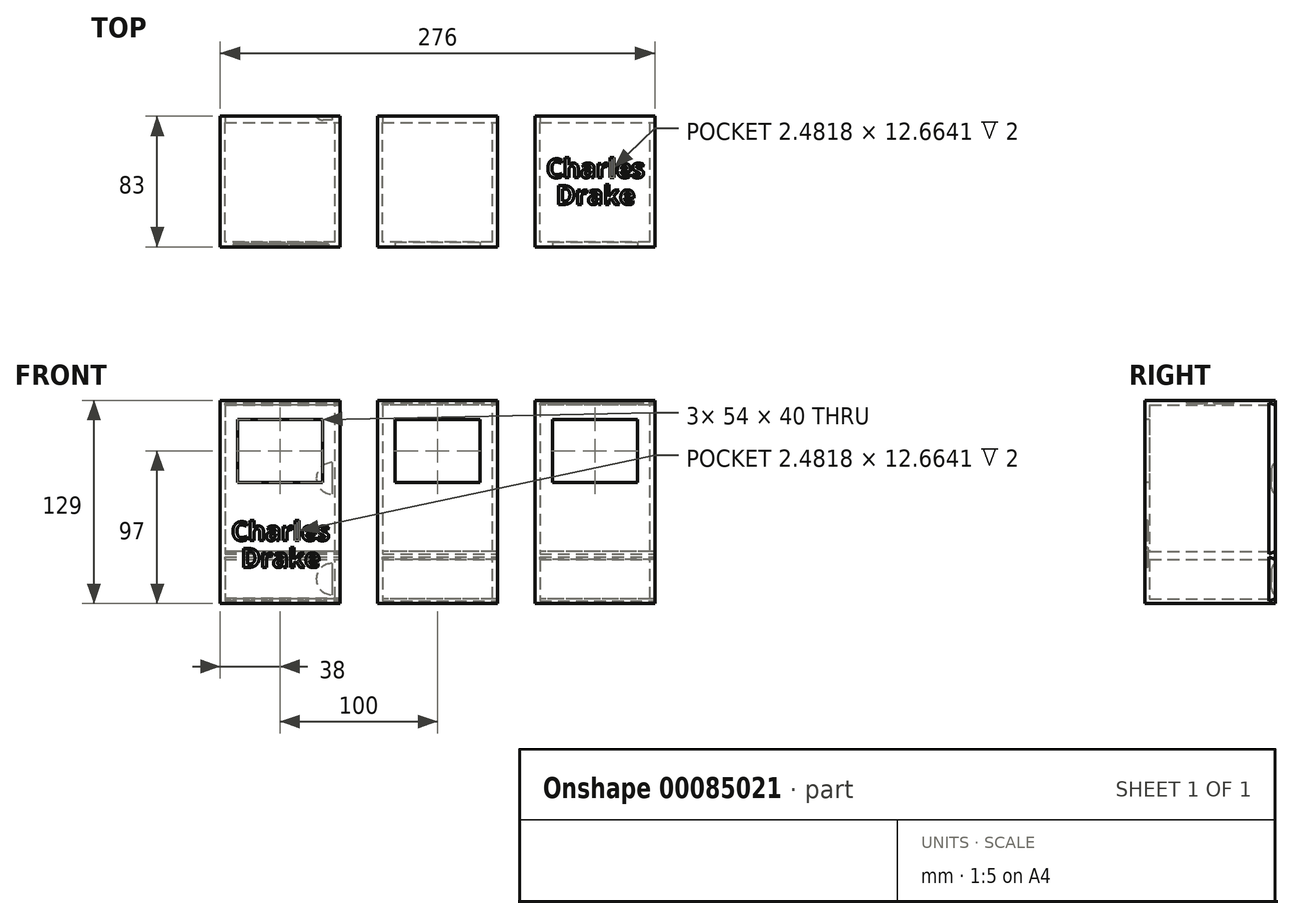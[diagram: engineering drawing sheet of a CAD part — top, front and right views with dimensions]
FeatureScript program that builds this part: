
annotation { "Feature Type Name" : "Feature", "Feature Type Description" : "" }
export const myFeature = defineFeature(function(context is Context, id is Id, definition is map)
    precondition{}
    {
        {
            var Q0;
            Q0=qCreatedBy(makeId("Top.planeOp"),FACE);
            var sketch = newSketch(context, id + "F0", { "sketchPlane" : qUnion([Q0])});
            skLineSegment(sketch, "E0.bottom", {"start": v(35, -38.5) * mm, "end": v(-35, -38.5) * mm});
            skLineSegment(sketch, "E0.top", {"start": v(35, 38.5) * mm, "end": v(-35, 38.5) * mm});
            skLineSegment(sketch, "E0.left", {"start": v(35, -38.5) * mm, "end": v(35, 38.5) * mm});
            skLineSegment(sketch, "E0.right", {"start": v(-35, -38.5) * mm, "end": v(-35, 38.5) * mm});
            skPoint(sketch, "E0.middle", {"position": v(0, 0) * mm});
            skLineSegment(sketch, "E1.0", {"start": v(38, 41.5) * mm, "end": v(-38, 41.5) * mm});
            skLineSegment(sketch, "E1.1", {"start": v(38, -41.5) * mm, "end": v(38, 41.5) * mm});
            skLineSegment(sketch, "E1.2", {"start": v(38, -41.5) * mm, "end": v(-38, -41.5) * mm});
            skLineSegment(sketch, "E1.3", {"start": v(-38, -41.5) * mm, "end": v(-38, 41.5) * mm});
            skSolve(sketch);
        }
        {
            var Q0;
            Q0=makeQuery(id+"F0.imprint","IMPRINT",FACE,{"disambiguationData":[TD([[makeQuery(id+"F0.imprint","IMPRINT",EDGE,{"derivedFrom":sQuery(id+"F0.wireOp",EDGE,"E0.bottom")}),-1.0]])]});
            var Q1;
            Q1=makeQuery(id+"F0.imprint","IMPRINT",FACE,{"disambiguationData":[TD([[makeQuery(id+"F0.imprint","IMPRINT",EDGE,{"derivedFrom":sQuery(id+"F0.wireOp",EDGE,"E0.bottom")}),1.0]])]});
            extrude(context, id + "F1", {"entities" : qUnion([Q0, Q1]), "depth" : 99 * mm});
        }
        {
            var Q0;
            Q0=makeQuery(id+"F1.opExtrude","SWEPT_FACE",FACE,{"disambiguationData":[OSD([sQuery(id+"F0.wireOp",EDGE,"E1.0")])]});
            shell(context, id + "F2", {"entities" : qUnion([Q0]), "thickness" : 3 * mm});
        }
        {
            var Q0;
            Q0=makeQuery(id+"F1.opExtrude","CAP_FACE",FACE,{"disambiguationData":[OSD([sQuery(id+"F0.wireOp",EDGE,"E1.0"),sQuery(id+"F0.wireOp",EDGE,"E1.1"),sQuery(id+"F0.wireOp",EDGE,"E1.2"),sQuery(id+"F0.wireOp",EDGE,"E1.3")])],"isStart":true});
            extrude(context, id + "F3", {"entities" : qUnion([Q0]), "operationType" : NewBodyOperationType.ADD, "depth" : 30 * mm});
        }
        {
            var Q0;
            {var subQ0=sQuery(id+"F0.wireOp",EDGE,"E1.0");Q0=makeQuery(id+"F3.boolean.opBoolean","MERGE",FACE,{"derivedFrom":[makeQuery(id+"F1.opExtrude","SWEPT_FACE",FACE,{"disambiguationData":[OSD([subQ0])]}),makeQuery(id+"F3.opExtrude","SWEPT_FACE",FACE,{"disambiguationData":[OSD([subQ0])]})]});}
            shell(context, id + "F4", {"entities" : qUnion([Q0]), "thickness" : 3 * mm});
        }
        {
            var Q0;
            {var subQ0=sQuery(id+"F0.wireOp",EDGE,"E1.2");Q0=makeQuery(id+"F3.boolean.opBoolean","MERGE",FACE,{"derivedFrom":[makeQuery(id+"F1.opExtrude","SWEPT_FACE",FACE,{"disambiguationData":[OSD([subQ0])]}),makeQuery(id+"F3.opExtrude","SWEPT_FACE",FACE,{"disambiguationData":[OSD([subQ0])]})]});}
            var sketch = newSketch(context, id + "F5", { "sketchPlane" : qUnion([Q0])});
            skLineSegment(sketch, "E2.0", {"start": v(35, 3) * mm, "end": v(-35, 3) * mm, "construction": true});
            skLineSegment(sketch, "E3", {"start": v(0, 99) * mm, "end": v(0, 3) * mm, "construction": true});
            skLineSegment(sketch, "E4.bottom", {"start": v(27, 47) * mm, "end": v(-27, 47) * mm});
            skLineSegment(sketch, "E4.top", {"start": v(27, 87) * mm, "end": v(-27, 87) * mm});
            skLineSegment(sketch, "E4.left", {"start": v(27, 47) * mm, "end": v(27, 87) * mm});
            skLineSegment(sketch, "E4.right", {"start": v(-27, 47) * mm, "end": v(-27, 87) * mm});
            skPoint(sketch, "E4.middle", {"position": v(0, 67) * mm});
            skSolve(sketch);
        }
        {
            var Q0;
            Q0=makeQuery(id+"F5.imprint","IMPRINT",FACE,{"disambiguationData":[TD([[makeQuery(id+"F5.imprint","IMPRINT",EDGE,{"derivedFrom":sQuery(id+"F5.wireOp",EDGE,"E4.bottom")}),-1.0]])]});
            extrude(context, id + "F6", {"entities" : qUnion([Q0]), "operationType" : NewBodyOperationType.REMOVE, "endBound" : BoundingType.UP_TO_NEXT, "oppositeDirection" : true, "depth" : 25 * mm});
        }
        {
            var Q0;
            {var subQ0=sQuery(id+"F0.wireOp",EDGE,"E1.1");Q0=makeQuery(id+"F3.boolean.opBoolean","MERGE",FACE,{"derivedFrom":[makeQuery(id+"F1.opExtrude","SWEPT_FACE",FACE,{"disambiguationData":[OSD([subQ0])]}),makeQuery(id+"F3.opExtrude","SWEPT_FACE",FACE,{"disambiguationData":[OSD([subQ0])]})]});}
            var sketch = newSketch(context, id + "F7", { "sketchPlane" : qUnion([Q0])});
            skLineSegment(sketch, "E5.0", {"start": v(-38.5, 96) * mm, "end": v(-38.5, 3) * mm, "construction": true});
            skLineSegment(sketch, "E6.0", {"start": v(-38.5, 3) * mm, "end": v(41.5, 3) * mm, "construction": true});
            skLineSegment(sketch, "E7.0", {"start": v(-38.5, 96) * mm, "end": v(41.5, 96) * mm, "construction": true});
            skLineSegment(sketch, "E8", {"start": v(37.5, 99) * mm, "end": v(37.5, -30) * mm, "construction": true});
            skLineSegment(sketch, "E9", {"start": v(41.5, 96) * mm, "end": v(37.5, 97.5) * mm});
            skLineSegment(sketch, "E10", {"start": v(37.5, 97.5) * mm, "end": v(37.5, 1.5) * mm});
            skLineSegment(sketch, "E11", {"start": v(37.5, 1.5) * mm, "end": v(41.5, 3) * mm});
            skSolve(sketch);
        }
        {
            var Q0;
            {var subQ0=sQuery(id+"F7.wireOp",EDGE,"E9");Q0=makeQuery(id+"F7.imprint","IMPRINT",FACE,{"disambiguationData":[TD([[makeQuery(id+"F7.imprint","IMPRINT",EDGE,{"derivedFrom":subQ0}),1.0]])]});}
            var Q1;
            Q1=makeQuery(id+"F2.opShell","OFFSET_FACE",FACE,{"disambiguationData":[OSD([sQuery(id+"F0.wireOp",EDGE,"E1.3")])]});
            extrude(context, id + "F8", {"entities" : qUnion([Q0]), "operationType" : NewBodyOperationType.REMOVE, "endBound" : BoundingType.UP_TO_SURFACE, "oppositeDirection" : true, "endBoundEntityFace" : qUnion([Q1]), "depth" : 25 * mm});
        }
        {
            var Q0;
            {var subQ0=sQuery(id+"F0.wireOp",EDGE,"E1.3");var subQ1=sQuery(id+"F0.wireOp",EDGE,"E1.2");var subQ2=sQuery(id+"F0.wireOp",EDGE,"E1.1");var subQ3=sQuery(id+"F0.wireOp",EDGE,"E1.0");Q0=makeQuery(id+"F4.opShell","OFFSET_FACE",FACE,{"disambiguationData":[OSD([subQ3,subQ2,subQ1,subQ0]),TDD([makeQuery(id+"F2.opShell","OFFSET_FACE",FACE,{"disambiguationData":[OSD([subQ3,subQ2,subQ1,subQ0]),TDD([makeQuery(id+"F1.opExtrude","CAP_FACE",FACE,{"disambiguationData":[OSD([subQ3,subQ2,subQ1,subQ0])],"isStart":true})])]})])]});}
            extrude(context, id + "F9", {"entities" : qUnion([Q0]), "operationType" : NewBodyOperationType.ADD, "depth" : 2 * mm});
        }
        {
            var Q0;
            {var subQ0=sQuery(id+"F0.wireOp",EDGE,"E1.1");Q0=makeQuery(id+"F3.boolean.opBoolean","MERGE",FACE,{"derivedFrom":[makeQuery(id+"F1.opExtrude","SWEPT_FACE",FACE,{"disambiguationData":[OSD([subQ0])]}),makeQuery(id+"F3.opExtrude","SWEPT_FACE",FACE,{"disambiguationData":[OSD([subQ0])]})]});}
            var sketch = newSketch(context, id + "F10", { "sketchPlane" : qUnion([Q0])});
            skLineSegment(sketch, "E12.0", {"start": v(-38.5, -2) * mm, "end": v(41.5, -2) * mm, "construction": true});
            skLineSegment(sketch, "E12.1", {"start": v(-38.5, -27) * mm, "end": v(41.5, -27) * mm, "construction": true});
            skLineSegment(sketch, "E13", {"start": v(37.5, 1.5) * mm, "end": v(37.5, -30) * mm, "construction": true});
            skLineSegment(sketch, "E14", {"start": v(41.5, -2) * mm, "end": v(37.5, -0.5) * mm});
            skLineSegment(sketch, "E15", {"start": v(37.5, -0.5) * mm, "end": v(37.5, -28.5) * mm});
            skLineSegment(sketch, "E16", {"start": v(37.5, -28.5) * mm, "end": v(41.5, -27) * mm});
            skSolve(sketch);
        }
        {
            var Q0;
            {var subQ0=sQuery(id+"F10.wireOp",EDGE,"E14");Q0=makeQuery(id+"F10.imprint","IMPRINT",FACE,{"disambiguationData":[TD([[makeQuery(id+"F10.imprint","IMPRINT",EDGE,{"derivedFrom":subQ0}),1.0]])]});}
            var Q1;
            Q1=makeQuery(id+"F4.opShell","OFFSET_FACE",FACE,{"disambiguationData":[OSD([sQuery(id+"F0.wireOp",EDGE,"E1.3")])]});
            extrude(context, id + "F11", {"entities" : qUnion([Q0]), "operationType" : NewBodyOperationType.REMOVE, "endBound" : BoundingType.UP_TO_SURFACE, "oppositeDirection" : true, "endBoundEntityFace" : qUnion([Q1]), "depth" : 25 * mm});
        }
        {
            var Q0;
            {var subQ0=sQuery(id+"F0.wireOp",EDGE,"E1.1");Q0=makeQuery(id+"F3.boolean.opBoolean","MERGE",FACE,{"derivedFrom":[makeQuery(id+"F1.opExtrude","SWEPT_FACE",FACE,{"disambiguationData":[OSD([subQ0])]}),makeQuery(id+"F3.opExtrude","SWEPT_FACE",FACE,{"disambiguationData":[OSD([subQ0])]})]});}
            var sketch = newSketch(context, id + "F12", { "sketchPlane" : qUnion([Q0])});
            skLineSegment(sketch, "E17", {"start": v(41.5, 96) * mm, "end": v(41.5, 3) * mm});
            skLineSegment(sketch, "E18", {"start": v(41.5, 3.5) * mm, "end": v(37.5, 2) * mm});
            skSolve(sketch);
        }
        {
            var Q0;
            {var subQ5=sQuery(id+"F12.wireOp",EDGE,"E18");Q0=makeQuery(id+"F12.imprint","IMPRINT",FACE,{"disambiguationData":[TD([[makeQuery(id+"F12.imprint","IMPRINT",EDGE,{"derivedFrom":subQ5}),-1.0]])]});}
            var Q1;
            {var subQ0=sQuery(id+"F0.wireOp",EDGE,"E1.3");Q1=makeQuery(id+"F8.boolean.opBoolean","MERGE",FACE,{"derivedFrom":[makeQuery(id+"F2.opShell","OFFSET_FACE",FACE,{"disambiguationData":[OSD([subQ0])]}),makeQuery(id+"F8.opExtrude","CAP_FACE",FACE,{"disambiguationData":[OSD([subQ0])],"isStart":false})]});}
            extrude(context, id + "F13", {"entities" : qUnion([Q0]), "endBound" : BoundingType.UP_TO_SURFACE, "oppositeDirection" : true, "endBoundEntityFace" : qUnion([Q1]), "depth" : 25 * mm});
        }
        {
            var Q0;
            {var subQ0=sQuery(id+"F0.wireOp",EDGE,"E1.1");Q0=makeQuery(id+"F3.boolean.opBoolean","MERGE",FACE,{"derivedFrom":[makeQuery(id+"F1.opExtrude","SWEPT_FACE",FACE,{"disambiguationData":[OSD([subQ0])]}),makeQuery(id+"F3.opExtrude","SWEPT_FACE",FACE,{"disambiguationData":[OSD([subQ0])]})]});}
            var sketch = newSketch(context, id + "F14", { "sketchPlane" : qUnion([Q0])});
            skLineSegment(sketch, "E19", {"start": v(41.5, -2) * mm, "end": v(41.5, -27) * mm});
            skLineSegment(sketch, "E20.0", {"start": v(37.5, -0.5) * mm, "end": v(37.5, -28.5) * mm});
            skLineSegment(sketch, "E21.0", {"start": v(41.5, -2) * mm, "end": v(37.5, -0.5) * mm});
            skLineSegment(sketch, "E22.0", {"start": v(37.5, -28.5) * mm, "end": v(41.5, -27) * mm});
            skLineSegment(sketch, "E23", {"start": v(41.5, -26.5) * mm, "end": v(37.5, -28) * mm});
            skSolve(sketch);
        }
        {
            var Q0;
            {var subQ0=sQuery(id+"F14.wireOp",EDGE,"E21.0");Q0=makeQuery(id+"F14.imprint","IMPRINT",FACE,{"disambiguationData":[TD([[makeQuery(id+"F14.imprint","IMPRINT",EDGE,{"derivedFrom":subQ0}),1.0]])]});}
            var Q1;
            {var subQ0=sQuery(id+"F0.wireOp",EDGE,"E1.3");Q1=makeQuery(id+"F11.boolean.opBoolean","MERGE",FACE,{"derivedFrom":[makeQuery(id+"F4.opShell","OFFSET_FACE",FACE,{"disambiguationData":[OSD([subQ0])]}),makeQuery(id+"F11.opExtrude","CAP_FACE",FACE,{"disambiguationData":[OSD([subQ0])],"isStart":false})]});}
            extrude(context, id + "F15", {"entities" : qUnion([Q0]), "endBound" : BoundingType.UP_TO_SURFACE, "oppositeDirection" : true, "endBoundEntityFace" : qUnion([Q1]), "depth" : 25 * mm});
        }
        {
            var Q0;
            Q0=makeQuery(id+"F13.opExtrude","SWEPT_FACE",FACE,{"disambiguationData":[OSD([sQuery(id+"F12.wireOp",EDGE,"E17")])]});
            var sketch = newSketch(context, id + "F16", { "sketchPlane" : qUnion([Q0])});
            skLineSegment(sketch, "E24", {"start": v(-38, 49.75) * mm, "end": v(35, 49.75) * mm, "construction": true});
            skLineSegment(sketch, "E25", {"start": v(35, 49.75) * mm, "end": v(35.14, 48.78) * mm, "construction": true});
            skLineSegment(sketch, "E26", {"start": v(-33, 96) * mm, "end": v(-33, 96) * mm});
            skArc(sketch, "E27", {"start": v(-33, 39.5) * mm, "mid": v(-23, 49.5) * mm, "end": v(-33, 59.5) * mm});
            skLineSegment(sketch, "E28", {"start": v(-33, 59.5) * mm, "end": v(-33, 39.5) * mm});
            skLineSegment(sketch, "E29.0", {"start": v(-38, -2) * mm, "end": v(35, -2) * mm});
            skLineSegment(sketch, "E30.0", {"start": v(-38, -27) * mm, "end": v(35, -27) * mm});
            skSolve(sketch);
        }
        {
            var Q0;
            Q0=makeQuery(id+"F16.imprint","IMPRINT",FACE,{"disambiguationData":[TD([[makeQuery(id+"F16.imprint","IMPRINT",EDGE,{"derivedFrom":sQuery(id+"F16.wireOp",EDGE,"E27")}),1.0]])]});
            var Q1;
            Q1=makeQuery(id+"F16.imprint","IMPRINT",FACE,{"disambiguationData":[TD([[makeQuery(id+"F16.imprint","IMPRINT",EDGE,{"derivedFrom":sQuery(id+"F16.wireOp",EDGE,"fAPIQIxa-ejnO-FiYm-n6jW-wiozmUmA0obh")}),1.0]])]});
            extrude(context, id + "F17", {"entities" : qUnion([Q0, Q1]), "operationType" : NewBodyOperationType.REMOVE, "oppositeDirection" : true, "depth" : 2.5 * mm});
        }
        {
            var Q0;
            Q0=makeQuery(id+"F17.boolean.opBoolean","COPY",EDGE,{"derivedFrom":makeQuery(id+"F17.opExtrude","CAP_EDGE",EDGE,{"disambiguationData":[OSD([sQuery(id+"F16.wireOp",EDGE,"E27")])],"isStart":false})});
            fillet(context, id + "F18", {"entities" : qUnion([Q0]), "radius" : 5 * mm, "tangentPropagation" : true, "allowEdgeOverflow" : false});
        }
        {
            var Q0;
            Q0=makeQuery(id+"F15.opExtrude","SWEPT_FACE",FACE,{"disambiguationData":[OSD([sQuery(id+"F14.wireOp",EDGE,"E19")])]});
            var sketch = newSketch(context, id + "F19", { "sketchPlane" : qUnion([Q0])});
            skLineSegment(sketch, "E31", {"start": v(-33, -2) * mm, "end": v(-33, -4.5) * mm, "construction": true});
            skArc(sketch, "E32", {"start": v(-33, -24.5) * mm, "mid": v(-23, -14.5) * mm, "end": v(-33, -4.5) * mm});
            skLineSegment(sketch, "E33", {"start": v(-33, -4.5) * mm, "end": v(-33, -24.5) * mm});
            skPoint(sketch, "E34.orphan", {"position": v(-33, -2) * mm});
            skSolve(sketch);
        }
        {
            var Q0;
            Q0=makeQuery(id+"F19.imprint","IMPRINT",FACE,{"disambiguationData":[TD([[makeQuery(id+"F19.imprint","IMPRINT",EDGE,{"derivedFrom":sQuery(id+"F19.wireOp",EDGE,"E32")}),1.0]])]});
            extrude(context, id + "F20", {"entities" : qUnion([Q0]), "operationType" : NewBodyOperationType.REMOVE, "oppositeDirection" : true, "depth" : 2.5 * mm});
        }
        {
            var Q0;
            Q0=makeQuery(id+"F20.boolean.opBoolean","COPY",EDGE,{"derivedFrom":makeQuery(id+"F20.opExtrude","CAP_EDGE",EDGE,{"disambiguationData":[OSD([sQuery(id+"F19.wireOp",EDGE,"E32")])],"isStart":false})});
            fillet(context, id + "F21", {"entities" : qUnion([Q0]), "radius" : 5 * mm, "tangentPropagation" : true, "allowEdgeOverflow" : false});
        }
        {
            var Q0;
            Q0=makeQuery(id+"F1.opExtrude","SWEPT_BODY",BODY,{"disambiguationData":[OSD([sQuery(id+"F0.wireOp",EDGE,"E1.0"),sQuery(id+"F0.wireOp",EDGE,"E1.1"),sQuery(id+"F0.wireOp",EDGE,"E1.2"),sQuery(id+"F0.wireOp",EDGE,"E1.3")])]});
            var Q1;
            {var subQ0=sQuery(id+"F0.wireOp",EDGE,"E1.1");Q1=makeQuery(id+"F3.boolean.opBoolean","MERGE",FACE,{"derivedFrom":[makeQuery(id+"F1.opExtrude","SWEPT_FACE",FACE,{"disambiguationData":[OSD([subQ0])]}),makeQuery(id+"F3.opExtrude","SWEPT_FACE",FACE,{"disambiguationData":[OSD([subQ0])]})]});}
            transform(context, id + "F22", {"entities" : qUnion([Q0]), "transformType" : TransformType.TRANSLATION_DISTANCE, "transformDirection" : qUnion([Q1]), "distance" : 100 * mm, "makeCopy" : true});
        }
        {
            var Q0;
            {var subQ0=sQuery(id+"F0.wireOp",EDGE,"E1.2");Q0=makeQuery(id+"F3.boolean.opBoolean","MERGE",FACE,{"derivedFrom":[makeQuery(id+"F1.opExtrude","SWEPT_FACE",FACE,{"disambiguationData":[OSD([subQ0])]}),makeQuery(id+"F3.opExtrude","SWEPT_FACE",FACE,{"disambiguationData":[OSD([subQ0])]})]});}
            var sketch = newSketch(context, id + "F23", { "sketchPlane" : qUnion([Q0])});
            skLineSegment(sketch, "E35", {"start": v(0, 99) * mm, "end": v(0, -30) * mm, "construction": true});
            skText(sketch, "E36", { "text": "Charles", "fontName": "OpenSans-Bold.ttf"});
            skText(sketch, "E37", { "text": "Drake", "fontName": "OpenSans-Bold.ttf"});
            const initialGuessF23  = {"E36": [-0.0309, 0.01, 1, 0, 0.012], "E37": [-0.02472, -0.007, 1, 0, 0.012]};
            skSetInitialGuess(sketch, initialGuessF23);
            skSolve(sketch);
        }
        {
            var Q0;
            Q0 = qSketchRegion(id + "F23", true);
            extrude(context, id + "F24", {"entities" : qUnion([Q0]), "operationType" : NewBodyOperationType.REMOVE, "oppositeDirection" : true, "depth" : 2 * mm});
        }
        {
            var Q0;
            Q0=makeQuery(id+"F22.opPattern","COPY",BODY,{"derivedFrom":makeQuery(id+"F1.opExtrude","SWEPT_BODY",BODY,{"disambiguationData":[OSD([sQuery(id+"F0.wireOp",EDGE,"E1.0"),sQuery(id+"F0.wireOp",EDGE,"E1.1"),sQuery(id+"F0.wireOp",EDGE,"E1.2"),sQuery(id+"F0.wireOp",EDGE,"E1.3")])]}),"instanceName":"1"});
            var Q1;
            {var subQ0=sQuery(id+"F0.wireOp",EDGE,"E1.1");Q1=makeQuery(id+"F22.opPattern","COPY",FACE,{"derivedFrom":makeQuery(id+"F3.boolean.opBoolean","MERGE",FACE,{"derivedFrom":[makeQuery(id+"F1.opExtrude","SWEPT_FACE",FACE,{"disambiguationData":[OSD([subQ0])]}),makeQuery(id+"F3.opExtrude","SWEPT_FACE",FACE,{"disambiguationData":[OSD([subQ0])]})]}),"instanceName":"1"});}
            transform(context, id + "F25", {"entities" : qUnion([Q0]), "transformType" : TransformType.TRANSLATION_DISTANCE, "transformDirection" : qUnion([Q1]), "distance" : 100 * mm, "makeCopy" : true});
        }
        {
            var Q0;
            Q0=makeQuery(id+"F25.opPattern","COPY",FACE,{"derivedFrom":makeQuery(id+"F22.opPattern","COPY",FACE,{"derivedFrom":makeQuery(id+"F1.opExtrude","CAP_FACE",FACE,{"disambiguationData":[OSD([sQuery(id+"F0.wireOp",EDGE,"E1.0"),sQuery(id+"F0.wireOp",EDGE,"E1.1"),sQuery(id+"F0.wireOp",EDGE,"E1.2"),sQuery(id+"F0.wireOp",EDGE,"E1.3")])],"isStart":false}),"instanceName":"1"}),"instanceName":"1"});
            var sketch = newSketch(context, id + "F26", { "sketchPlane" : qUnion([Q0])});
            skLineSegment(sketch, "E38", {"start": v(200, 41.5) * mm, "end": v(200, -41.5) * mm, "construction": true});
            skText(sketch, "E39", { "text": "Charles", "fontName": "OpenSans-Bold.ttf"});
            skText(sketch, "E40", { "text": "Drake", "fontName": "OpenSans-Bold.ttf"});
            const initialGuessF26  = {"E39": [0.1691, 0.0025, 1, 0, 0.012], "E40": [0.17528, -0.0145, 1, 0, 0.012]};
            skSetInitialGuess(sketch, initialGuessF26);
            skSolve(sketch);
        }
        {
            var Q0;
            Q0 = qSketchRegion(id + "F26", true);
            extrude(context, id + "F27", {"entities" : qUnion([Q0]), "operationType" : NewBodyOperationType.REMOVE, "oppositeDirection" : true, "depth" : 2 * mm});
        }
    });
